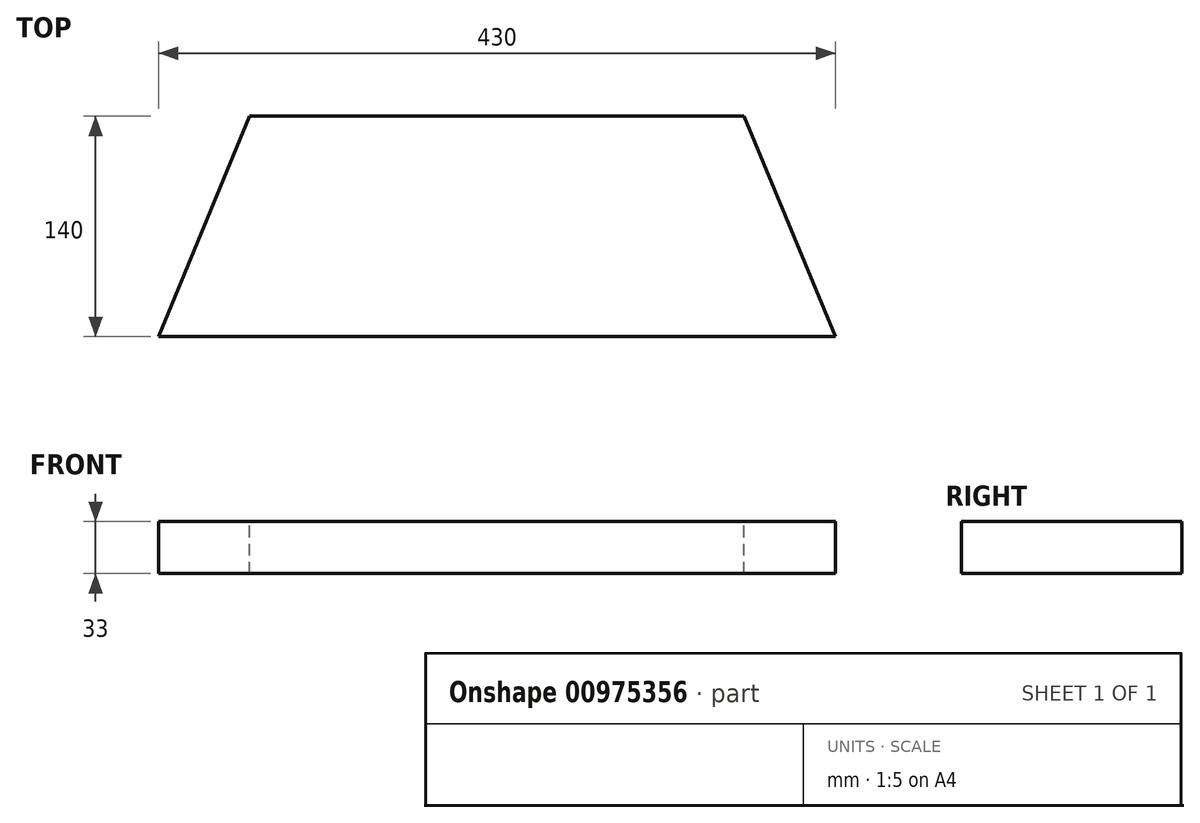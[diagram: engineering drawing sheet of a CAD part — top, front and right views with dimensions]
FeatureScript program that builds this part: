
annotation { "Feature Type Name" : "Feature", "Feature Type Description" : "" }
export const myFeature = defineFeature(function(context is Context, id is Id, definition is map)
    precondition{}
    {
        {
            var Q0;
            Q0=qCreatedBy(makeId("Top.planeOp"),FACE);
            var sketch = newSketch(context, id + "F0", { "sketchPlane" : qUnion([Q0])});
            skLineSegment(sketch, "E0.bottom", {"start": v(215, 70) * mm, "end": v(-215, 70) * mm});
            skLineSegment(sketch, "E0.top", {"start": v(215, -70) * mm, "end": v(-215, -70) * mm});
            skLineSegment(sketch, "E0.left", {"start": v(215, 70) * mm, "end": v(215, -70) * mm});
            skLineSegment(sketch, "E0.right", {"start": v(-215, 70) * mm, "end": v(-215, -70) * mm});
            skPoint(sketch, "E0.middle", {"position": v(0, 0) * mm});
            skSolve(sketch);
        }
        {
            var Q0;
            Q0=makeQuery(id+"F0.imprint","IMPRINT",FACE,{"disambiguationData":[TD([[makeQuery(id+"F0.imprint","IMPRINT",EDGE,{"derivedFrom":sQuery(id+"F0.wireOp",EDGE,"E0.bottom")}),1.0]])]});
            extrude(context, id + "F1", {"entities" : qUnion([Q0]), "endBound" : BoundingType.SYMMETRIC, "depth" : 33 * mm, "offsetDistance" : 25 * mm});
        }
        {
            var Q0;
            Q0=makeQuery(id+"F1.opExtrude","CAP_FACE",FACE,{"disambiguationData":[OSD([sQuery(id+"F0.wireOp",EDGE,"E0.bottom"),sQuery(id+"F0.wireOp",EDGE,"E0.top"),sQuery(id+"F0.wireOp",EDGE,"E0.left"),sQuery(id+"F0.wireOp",EDGE,"E0.right")])],"isStart":false});
            var sketch = newSketch(context, id + "F2", { "sketchPlane" : qUnion([Q0])});
            skLineSegment(sketch, "E1", {"start": v(-215, -70) * mm, "end": v(-157.01, 70) * mm});
            skLineSegment(sketch, "E2", {"start": v(-157.01, 70) * mm, "end": v(-215, 70) * mm});
            skLineSegment(sketch, "E3", {"start": v(-215, 70) * mm, "end": v(-215, -70) * mm});
            skLineSegment(sketch, "E4", {"start": v(215, 70) * mm, "end": v(157.01, 70) * mm});
            skLineSegment(sketch, "E5", {"start": v(157.01, 70) * mm, "end": v(215, -70) * mm});
            skLineSegment(sketch, "E6", {"start": v(215, -70) * mm, "end": v(215, 70) * mm});
            skSolve(sketch);
        }
        {
            var Q0;
            Q0=qSketchRegion(id+"F2",true);
            extrude(context, id + "F3", {"entities" : qUnion([Q0]), "operationType" : NewBodyOperationType.REMOVE, "endBound" : BoundingType.THROUGH_ALL, "oppositeDirection" : true, "depth" : 25 * mm, "offsetDistance" : 25 * mm});
        }
    });
